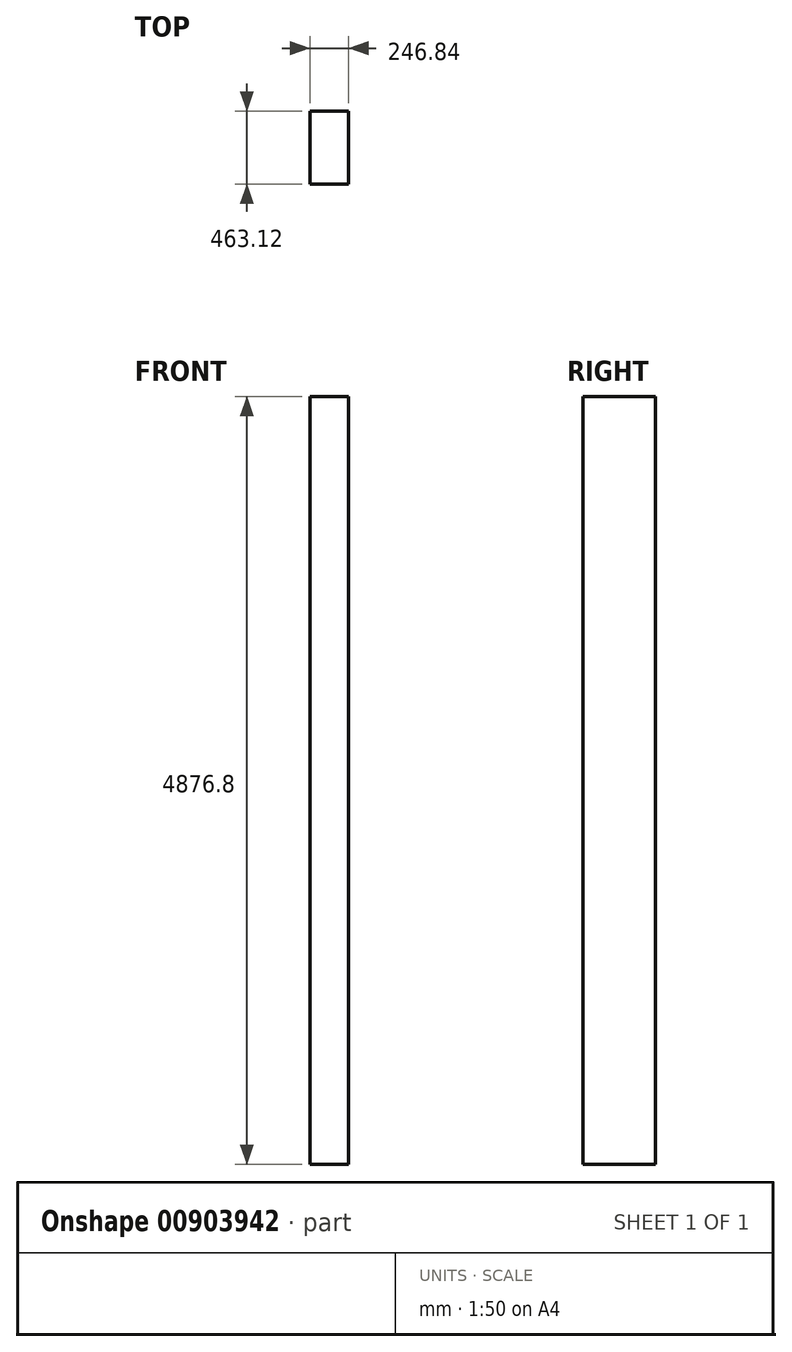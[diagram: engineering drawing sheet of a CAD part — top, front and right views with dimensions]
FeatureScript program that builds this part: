
annotation { "Feature Type Name" : "Feature", "Feature Type Description" : "" }
export const myFeature = defineFeature(function(context is Context, id is Id, definition is map)
    precondition{}
    {
        {
            var Q0;
            Q0=qCreatedBy(makeId("Top.planeOp"),FACE);
            var sketch = newSketch(context, id + "F0", { "sketchPlane" : qUnion([Q0])});
            skLineSegment(sketch, "E0.bottom", {"start": v(123.42, 231.56) * mm, "end": v(-123.42, 231.56) * mm});
            skLineSegment(sketch, "E0.top", {"start": v(123.42, -231.56) * mm, "end": v(-123.42, -231.56) * mm});
            skLineSegment(sketch, "E0.left", {"start": v(123.42, 231.56) * mm, "end": v(123.42, -231.56) * mm});
            skLineSegment(sketch, "E0.right", {"start": v(-123.42, 231.56) * mm, "end": v(-123.42, -231.56) * mm});
            skPoint(sketch, "E0.middle", {"position": v(0, 0) * mm});
            skSolve(sketch);
        }
        {
            var Q0;
            Q0=makeQuery(id+"F0.imprint","IMPRINT",FACE,{"disambiguationData":[TD([[makeQuery(id+"F0.imprint","IMPRINT",EDGE,{"derivedFrom":sQuery(id+"F0.wireOp",EDGE,"E0.bottom")}),1.0]])]});
            extrude(context, id + "F1", {"entities" : qUnion([Q0]), "depth" : 4876.8 * mm, "offsetDistance" : 25.4 * mm});
        }
    });
